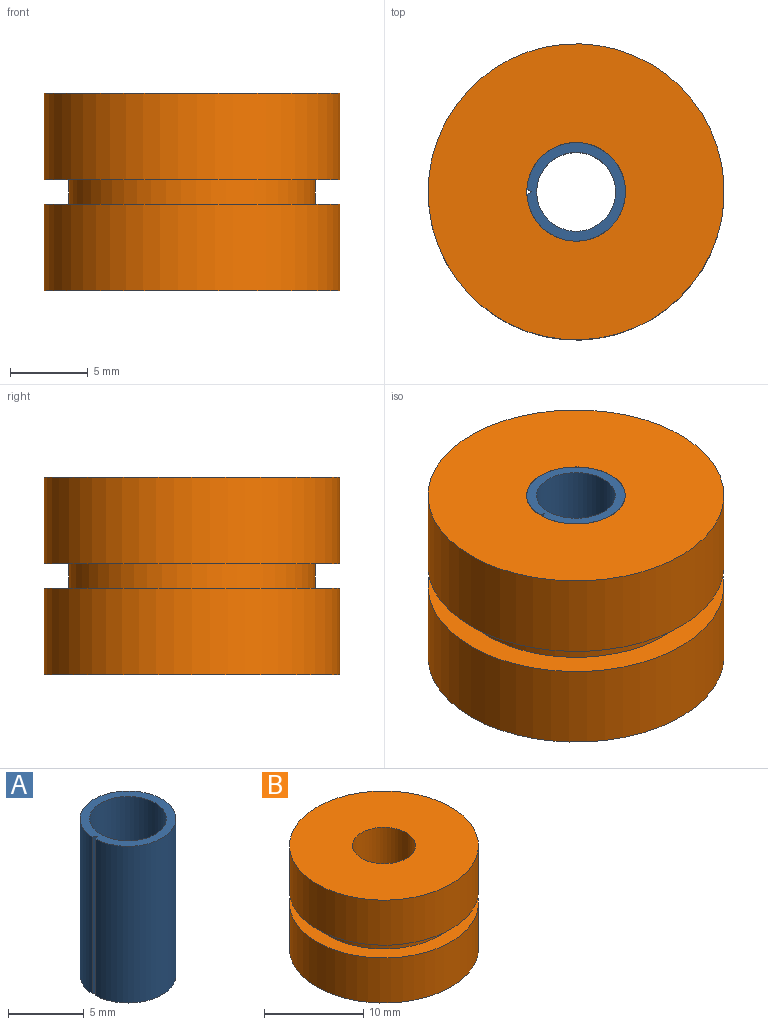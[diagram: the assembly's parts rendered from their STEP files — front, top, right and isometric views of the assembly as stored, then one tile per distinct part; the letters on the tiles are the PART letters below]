
ASSEMBLY  parts=2 mates=1
PART A: 6 faces, bbox 6.3x6.4x12.7 mm
  f0: plane 12.7x0.3mm, normal (-0.5,-0.87,0), area 4.4mm2, adj f1,f3,f4,f5
  f1: plane 12.7x0.3mm, normal (-0.5,0.87,0), area 4.4mm2, adj f0,f3,f4,f5
  f2: cylinder r=2.54mm len=12.7mm, axis (0,0,-1), area 202.7mm2, adj f4,f5
  f3: cylinder r=3.17mm len=12.7mm, axis (0,0,-1), area 249mm2, adj f0,f1,f4,f5
  f4: plane 6.35x6.35mm, normal (0,0,1), area 11.3mm2, adj f0,f1,f2,f3
  f5: plane 6.35x6.35mm, normal (0,0,-1), area 11.3mm2, adj f0,f1,f2,f3
PART B: 8 faces, bbox 19.1x19.1x12.7 mm
  f0: cylinder r=9.53mm len=19.05mm, axis (0,0,-1), area 332.5mm2, adj f1,f7
  f1: plane 19.05x19.05mm, normal (0,0,-1), area 253.4mm2, adj f0,f2
  f2: cylinder r=3.17mm len=12.7mm, axis (0,0,-1), area 253.4mm2, adj f1,f3
  f3: plane 19.05x19.05mm, normal (0,0,1), area 253.4mm2, adj f2,f4
  f4: cylinder r=9.53mm len=19.05mm, axis (0,0,-1), area 332.5mm2, adj f3,f5
  f5: plane 19.05x19.05mm, normal (0,0,-1), area 87.1mm2, adj f4,f6
  f6: cylinder r=7.94mm len=15.88mm, axis (0,0,-1), area 79.2mm2, adj f5,f7
  f7: plane 19.05x19.05mm, normal (0,0,1), area 87.1mm2, adj f0,f6
PLACE A t=(-3.08,-4.01,0.08)mm
PLACE B t=(-3.08,-4.01,5.64)mm
MATE fastened B.f0 <-> A.f2  axis (0,0,-1) through (-3.08,-4.01,6.43)mm
